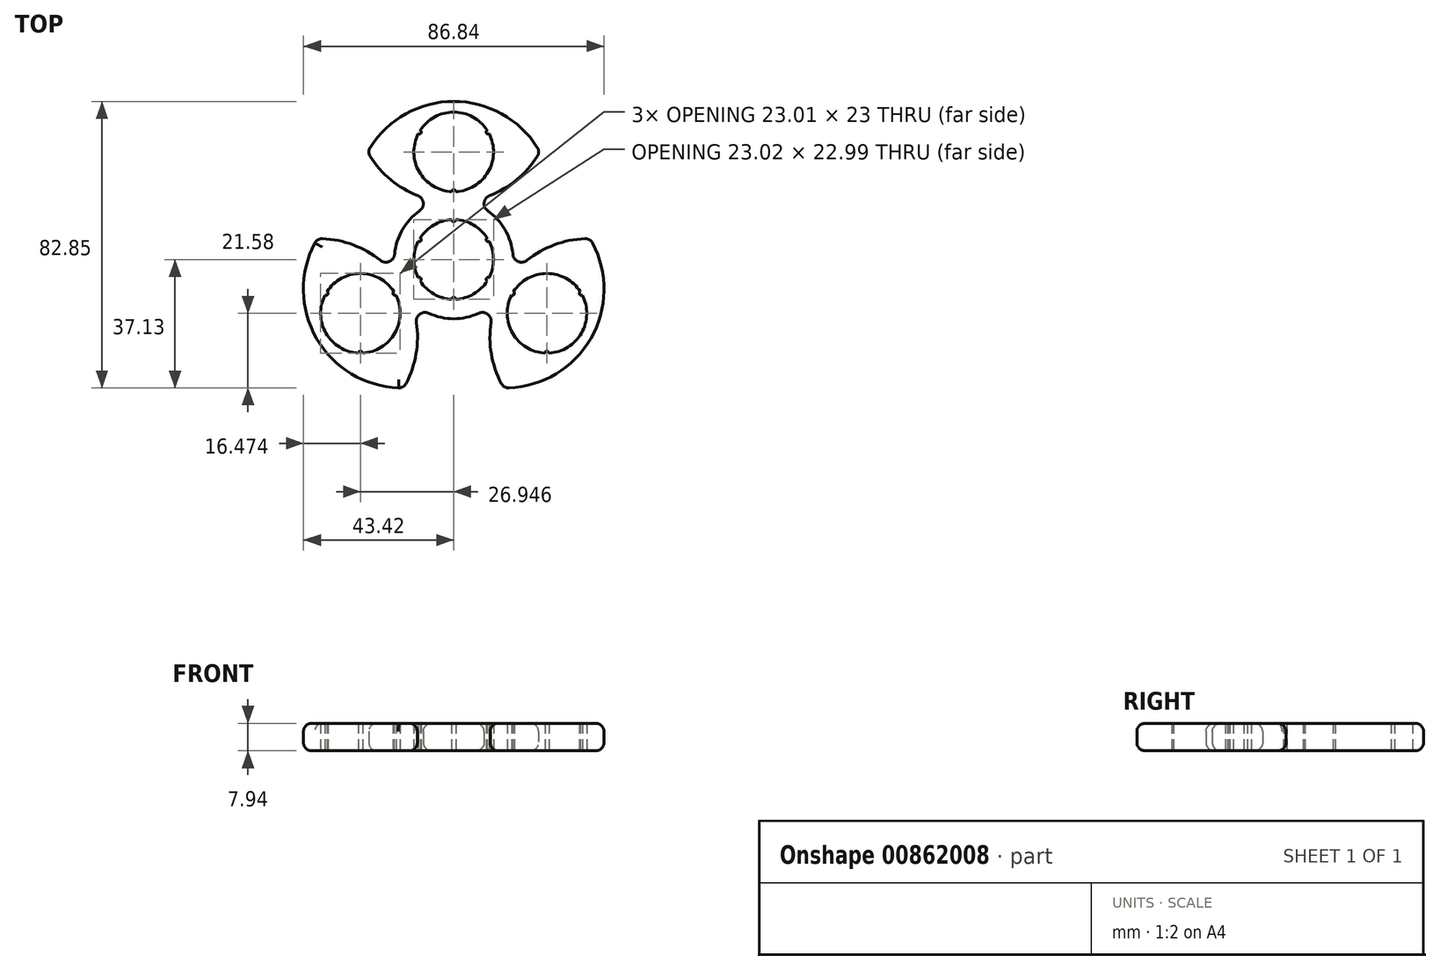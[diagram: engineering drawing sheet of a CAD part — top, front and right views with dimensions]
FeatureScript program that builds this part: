
annotation { "Feature Type Name" : "Feature", "Feature Type Description" : "" }
export const myFeature = defineFeature(function(context is Context, id is Id, definition is map)
    precondition{}
    {
        {
            var Q0;
            Q0=qCreatedBy(makeId("Top.planeOp"),FACE);
            var sketch = newSketch(context, id + "F0", { "sketchPlane" : qUnion([Q0])});
            skCircle(sketch, "E0", {"center": v(0, 0) * mm, "radius": 45.72 * mm, "construction": true});
            skLineSegment(sketch, "E1", {"start": v(0, 0) * mm, "end": v(0, 90.17) * mm, "construction": true});
            skLineSegment(sketch, "E2", {"start": v(0, 0) * mm, "end": v(-73.93, -42.68) * mm, "construction": true});
            skLineSegment(sketch, "E3", {"start": v(0, 0) * mm, "end": v(66.36, -38.31) * mm, "construction": true});
            skArc(sketch, "E4", {"start": v(9.66, 37.37) * mm, "mid": v(0, 42.62) * mm, "end": v(-9.66, 37.37) * mm});
            skArc(sketch, "E5", {"start": v(-0.59, 11.5) * mm, "mid": v(-5.75, 9.97) * mm, "end": v(-9.66, 6.26) * mm});
            skPoint(sketch, "E6", {"position": v(0, 17.14) * mm});
            skArc(sketch, "E7", {"start": v(24.93, 31.12) * mm, "mid": v(0, 45.72) * mm, "end": v(-24.93, 31.12) * mm});
            skPoint(sketch, "E8", {"position": v(0, 45.09) * mm});
            skArc(sketch, "E9", {"start": v(-24.93, 31.12) * mm, "mid": v(-18.76, 23.53) * mm, "end": v(-10.4, 18.47) * mm});
            skLineSegment(sketch, "E10", {"start": v(-41.52, 31.12) * mm, "end": v(42.77, 31.12) * mm, "construction": true});
            skArc(sketch, "E11", {"start": v(-9.86, 14.03) * mm, "mid": v(-14.85, 8.57) * mm, "end": v(-17.08, 1.53) * mm});
            skArc(sketch, "E12.1.0", {"start": v(-39.41, 6.03) * mm, "mid": v(-39.6, -22.86) * mm, "end": v(-14.48, -37.15) * mm});
            skArc(sketch, "E12.1.1", {"start": v(-17.29, -9.3) * mm, "mid": v(-26.95, -4.05) * mm, "end": v(-36.6, -9.3) * mm});
            skArc(sketch, "E12.1.2", {"start": v(-14.48, -37.15) * mm, "mid": v(-11, -28.01) * mm, "end": v(-10.8, -18.24) * mm});
            skArc(sketch, "E12.2.0", {"start": v(14.48, -37.15) * mm, "mid": v(39.6, -22.86) * mm, "end": v(39.41, 6.03) * mm});
            skArc(sketch, "E12.2.1", {"start": v(16.7, -10.32) * mm, "mid": v(16.98, -21.31) * mm, "end": v(26.36, -27.05) * mm});
            skArc(sketch, "E12.2.2", {"start": v(39.41, 6.03) * mm, "mid": v(29.76, 4.48) * mm, "end": v(21.2, -0.23) * mm});
            skArc(sketch, "E13.trimOffspring", {"start": v(10.4, 18.47) * mm, "mid": v(18.76, 23.53) * mm, "end": v(24.93, 31.12) * mm});
            skArc(sketch, "E14.trimOffspring", {"start": v(17.08, 1.53) * mm, "mid": v(14.85, 8.57) * mm, "end": v(9.86, 14.03) * mm});
            skArc(sketch, "E15.trimOffspring", {"start": v(10.8, -18.24) * mm, "mid": v(11, -28.01) * mm, "end": v(14.48, -37.15) * mm});
            skArc(sketch, "E16.trimOffspring", {"start": v(-21.2, -0.23) * mm, "mid": v(-29.76, 4.48) * mm, "end": v(-39.41, 6.03) * mm});
            skArc(sketch, "E17.trimOffspring", {"start": v(-7.22, -15.55) * mm, "mid": v(0, -17.15) * mm, "end": v(7.22, -15.55) * mm});
            skPoint(sketch, "E18.visualSharp", {"position": v(-3.67, 16.75) * mm});
            skArc(sketch, "E18.filletArc", {"start": v(-9.86, 14.03) * mm, "mid": v(-8.8, 16.4) * mm, "end": v(-10.4, 18.47) * mm});
            skPoint(sketch, "E19.visualSharp", {"position": v(3.67, 16.75) * mm});
            skArc(sketch, "E19.filletArc", {"start": v(10.4, 18.47) * mm, "mid": v(8.8, 16.4) * mm, "end": v(9.86, 14.03) * mm});
            skPoint(sketch, "E20.visualSharp", {"position": v(16.34, -5.2) * mm});
            skArc(sketch, "E20.filletArc", {"start": v(17.08, 1.53) * mm, "mid": v(18.6, -0.58) * mm, "end": v(21.2, -0.23) * mm});
            skPoint(sketch, "E21.visualSharp", {"position": v(12.67, -11.55) * mm});
            skArc(sketch, "E21.filletArc", {"start": v(10.8, -18.24) * mm, "mid": v(9.8, -15.83) * mm, "end": v(7.22, -15.55) * mm});
            skPoint(sketch, "E22.visualSharp", {"position": v(-12.67, -11.55) * mm});
            skArc(sketch, "E22.filletArc", {"start": v(-7.22, -15.55) * mm, "mid": v(-9.8, -15.83) * mm, "end": v(-10.8, -18.24) * mm});
            skPoint(sketch, "E23.visualSharp", {"position": v(-16.34, -5.2) * mm});
            skArc(sketch, "E23.filletArc", {"start": v(-21.2, -0.23) * mm, "mid": v(-18.6, -0.58) * mm, "end": v(-17.08, 1.53) * mm});
            skLineSegment(sketch, "E24", {"start": v(0, 31.12) * mm, "end": v(-25.28, 45.7) * mm, "construction": true});
            skLineSegment(sketch, "E25", {"start": v(0, 31.11) * mm, "end": v(24.72, 45.39) * mm, "construction": true});
            skCircle(sketch, "E26", {"center": v(0, 31.12) * mm, "radius": 10.92 * mm, "construction": true});
            skArc(sketch, "E27", {"start": v(0.59, 19.62) * mm, "mid": v(0, 20.2) * mm, "end": v(-0.59, 19.62) * mm});
            skArc(sketch, "E28", {"start": v(-10.25, 36.35) * mm, "mid": v(-9.46, 36.58) * mm, "end": v(-9.66, 37.37) * mm});
            skArc(sketch, "E29", {"start": v(9.66, 37.37) * mm, "mid": v(9.46, 36.58) * mm, "end": v(10.25, 36.35) * mm});
            skArc(sketch, "E30.1.0", {"start": v(-26.36, -27.05) * mm, "mid": v(-26.95, -26.48) * mm, "end": v(-27.53, -27.05) * mm});
            skArc(sketch, "E30.1.1", {"start": v(-37.2, -10.32) * mm, "mid": v(-36.4, -10.1) * mm, "end": v(-36.6, -9.3) * mm});
            skArc(sketch, "E30.1.2", {"start": v(-17.29, -9.3) * mm, "mid": v(-17.49, -10.1) * mm, "end": v(-16.7, -10.32) * mm});
            skArc(sketch, "E30.2.0", {"start": v(36.6, -9.3) * mm, "mid": v(36.4, -10.1) * mm, "end": v(37.2, -10.32) * mm});
            skArc(sketch, "E30.2.1", {"start": v(27.53, -27.05) * mm, "mid": v(26.95, -26.48) * mm, "end": v(26.36, -27.05) * mm});
            skArc(sketch, "E30.2.2", {"start": v(16.7, -10.32) * mm, "mid": v(17.49, -10.1) * mm, "end": v(17.29, -9.3) * mm});
            skArc(sketch, "E31.trimOffspring", {"start": v(-10.25, 36.35) * mm, "mid": v(-9.97, 25.36) * mm, "end": v(-0.59, 19.62) * mm});
            skArc(sketch, "E32.trimOffspring", {"start": v(0.59, 19.62) * mm, "mid": v(9.97, 25.36) * mm, "end": v(10.25, 36.35) * mm});
            skArc(sketch, "E33.trimOffspring", {"start": v(-37.2, -10.32) * mm, "mid": v(-36.91, -21.31) * mm, "end": v(-27.53, -27.05) * mm});
            skArc(sketch, "E34.trimOffspring", {"start": v(-26.36, -27.05) * mm, "mid": v(-16.98, -21.31) * mm, "end": v(-16.7, -10.32) * mm});
            skArc(sketch, "E35.trimOffspring", {"start": v(36.6, -9.3) * mm, "mid": v(26.95, -4.05) * mm, "end": v(17.29, -9.3) * mm});
            skArc(sketch, "E36.trimOffspring", {"start": v(27.53, -27.05) * mm, "mid": v(36.91, -21.31) * mm, "end": v(37.2, -10.32) * mm});
            skCircle(sketch, "E37", {"center": v(0, 0) * mm, "radius": 10.92 * mm, "construction": true});
            skArc(sketch, "E38", {"start": v(-0.59, 11.5) * mm, "mid": v(0, 10.92) * mm, "end": v(0.59, 11.5) * mm});
            skArc(sketch, "E39.1.0", {"start": v(-10.25, 5.24) * mm, "mid": v(-9.46, 5.46) * mm, "end": v(-9.66, 6.26) * mm});
            skArc(sketch, "E39.2.0", {"start": v(-9.66, -6.26) * mm, "mid": v(-9.46, -5.46) * mm, "end": v(-10.25, -5.24) * mm});
            skArc(sketch, "E39.3.0", {"start": v(0.59, -11.5) * mm, "mid": v(0, -10.92) * mm, "end": v(-0.59, -11.5) * mm});
            skArc(sketch, "E39.4.0", {"start": v(10.25, -5.24) * mm, "mid": v(9.46, -5.46) * mm, "end": v(9.66, -6.26) * mm});
            skArc(sketch, "E39.5.0", {"start": v(9.66, 6.26) * mm, "mid": v(9.46, 5.46) * mm, "end": v(10.25, 5.24) * mm});
            skArc(sketch, "E40.trimOffspring", {"start": v(9.66, 6.26) * mm, "mid": v(5.75, 9.97) * mm, "end": v(0.59, 11.5) * mm});
            skArc(sketch, "E41.trimOffspring", {"start": v(10.25, -5.24) * mm, "mid": v(11.5, 0) * mm, "end": v(10.25, 5.24) * mm});
            skArc(sketch, "E42.trimOffspring", {"start": v(0.59, -11.5) * mm, "mid": v(5.75, -9.97) * mm, "end": v(9.66, -6.26) * mm});
            skArc(sketch, "E43.trimOffspring", {"start": v(-9.66, -6.26) * mm, "mid": v(-5.75, -9.97) * mm, "end": v(-0.59, -11.5) * mm});
            skArc(sketch, "E44.trimOffspring", {"start": v(-10.25, 5.24) * mm, "mid": v(-11.5, 0) * mm, "end": v(-10.25, -5.24) * mm});
            skSolve(sketch);
        }
        {
            var Q0;
            Q0 = qSketchRegion(id + "F0", true);
            extrude(context, id + "F1", {"entities" : qUnion([Q0]), "depth" : 7.94 * mm, "offsetDistance" : 25.4 * mm});
        }
        {
            var Q0;
            Q0=makeQuery(id+"F1.opExtrude","CAP_EDGE",EDGE,{"disambiguationData":[OSD([sQuery(id+"F0.wireOp",EDGE,"E12.1.0")])],"isStart":false});
            fillet(context, id + "F2", {"entities" : qUnion([Q0]), "radius" : 2.38 * mm, "tangentPropagation" : true, "allowEdgeOverflow" : false});
        }
        {
            var Q0;
            Q0=makeQuery(id+"F1.opExtrude","CAP_EDGE",EDGE,{"disambiguationData":[OSD([sQuery(id+"F0.wireOp",EDGE,"E12.1.2")])],"isStart":false});
            var Q1;
            Q1=makeQuery(id+"F1.opExtrude","CAP_EDGE",EDGE,{"disambiguationData":[OSD([sQuery(id+"F0.wireOp",EDGE,"E22.filletArc")])],"isStart":false});
            var Q2;
            Q2=makeQuery(id+"F1.opExtrude","CAP_EDGE",EDGE,{"disambiguationData":[OSD([sQuery(id+"F0.wireOp",EDGE,"E17.trimOffspring")])],"isStart":false});
            var Q3;
            Q3=makeQuery(id+"F1.opExtrude","CAP_EDGE",EDGE,{"disambiguationData":[OSD([sQuery(id+"F0.wireOp",EDGE,"E21.filletArc")])],"isStart":false});
            var Q4;
            Q4=makeQuery(id+"F1.opExtrude","CAP_EDGE",EDGE,{"disambiguationData":[OSD([sQuery(id+"F0.wireOp",EDGE,"E15.trimOffspring")])],"isStart":false});
            var Q5;
            Q5=makeQuery(id+"F1.opExtrude","CAP_EDGE",EDGE,{"disambiguationData":[OSD([sQuery(id+"F0.wireOp",EDGE,"E12.2.0")])],"isStart":false});
            var Q6;
            Q6=makeQuery(id+"F1.opExtrude","CAP_EDGE",EDGE,{"disambiguationData":[OSD([sQuery(id+"F0.wireOp",EDGE,"E12.2.2")])],"isStart":false});
            var Q7;
            Q7=makeQuery(id+"F1.opExtrude","CAP_EDGE",EDGE,{"disambiguationData":[OSD([sQuery(id+"F0.wireOp",EDGE,"E20.filletArc")])],"isStart":false});
            var Q8;
            Q8=makeQuery(id+"F1.opExtrude","CAP_EDGE",EDGE,{"disambiguationData":[OSD([sQuery(id+"F0.wireOp",EDGE,"E14.trimOffspring")])],"isStart":false});
            var Q9;
            Q9=makeQuery(id+"F1.opExtrude","CAP_EDGE",EDGE,{"disambiguationData":[OSD([sQuery(id+"F0.wireOp",EDGE,"E19.filletArc")])],"isStart":false});
            var Q10;
            Q10=makeQuery(id+"F1.opExtrude","CAP_EDGE",EDGE,{"disambiguationData":[OSD([sQuery(id+"F0.wireOp",EDGE,"E13.trimOffspring")])],"isStart":false});
            var Q11;
            Q11=makeQuery(id+"F1.opExtrude","CAP_EDGE",EDGE,{"disambiguationData":[OSD([sQuery(id+"F0.wireOp",EDGE,"E7")])],"isStart":false});
            var Q12;
            Q12=makeQuery(id+"F1.opExtrude","CAP_EDGE",EDGE,{"disambiguationData":[OSD([sQuery(id+"F0.wireOp",EDGE,"E9")])],"isStart":false});
            var Q13;
            Q13=makeQuery(id+"F1.opExtrude","CAP_EDGE",EDGE,{"disambiguationData":[OSD([sQuery(id+"F0.wireOp",EDGE,"E18.filletArc")])],"isStart":false});
            var Q14;
            Q14=makeQuery(id+"F1.opExtrude","CAP_EDGE",EDGE,{"disambiguationData":[OSD([sQuery(id+"F0.wireOp",EDGE,"E11")])],"isStart":false});
            var Q15;
            Q15=makeQuery(id+"F1.opExtrude","CAP_EDGE",EDGE,{"disambiguationData":[OSD([sQuery(id+"F0.wireOp",EDGE,"E23.filletArc")])],"isStart":false});
            var Q16;
            Q16=makeQuery(id+"F1.opExtrude","CAP_EDGE",EDGE,{"disambiguationData":[OSD([sQuery(id+"F0.wireOp",EDGE,"E16.trimOffspring")])],"isStart":false});
            fillet(context, id + "F3", {"entities" : qUnion([Q0, Q1, Q2, Q3, Q4, Q5, Q6, Q7, Q8, Q9, Q10, Q11, Q12, Q13, Q14, Q15, Q16]), "radius" : 2.38 * mm, "tangentPropagation" : true, "allowEdgeOverflow" : false});
        }
        {
            var Q0;
            Q0=makeQuery(id+"F1.opExtrude","CAP_EDGE",EDGE,{"disambiguationData":[OSD([sQuery(id+"F0.wireOp",EDGE,"E12.1.0")])],"isStart":true});
            var Q1;
            {var subQ0=sQuery(id+"F0.wireOp",EDGE,"E16.trimOffspring");var subQ1=sQuery(id+"F0.wireOp",EDGE,"E12.1.0");Q1=makeQuery(id+"F3.opFillet","BLEND_EDGE",EDGE,{"blendedFrom":[makeQuery(id+"F1.opExtrude","SWEPT_EDGE",EDGE,{"disambiguationData":[OSD([subQ1,subQ0])]}),makeQuery(id+"F1.opExtrude","CAP_FACE",FACE,{"disambiguationData":[OSD([sQuery(id+"F0.wireOp",EDGE,"E4"),sQuery(id+"F0.wireOp",EDGE,"E5"),sQuery(id+"F0.wireOp",EDGE,"E7"),sQuery(id+"F0.wireOp",EDGE,"E9"),sQuery(id+"F0.wireOp",EDGE,"E11"),subQ1,sQuery(id+"F0.wireOp",EDGE,"E12.1.1"),sQuery(id+"F0.wireOp",EDGE,"E12.1.2"),sQuery(id+"F0.wireOp",EDGE,"E12.2.0"),sQuery(id+"F0.wireOp",EDGE,"E12.2.1"),sQuery(id+"F0.wireOp",EDGE,"E12.2.2"),sQuery(id+"F0.wireOp",EDGE,"E13.trimOffspring"),sQuery(id+"F0.wireOp",EDGE,"E14.trimOffspring"),sQuery(id+"F0.wireOp",EDGE,"E15.trimOffspring"),subQ0,sQuery(id+"F0.wireOp",EDGE,"E17.trimOffspring"),sQuery(id+"F0.wireOp",EDGE,"E18.filletArc"),sQuery(id+"F0.wireOp",EDGE,"E19.filletArc"),sQuery(id+"F0.wireOp",EDGE,"E20.filletArc"),sQuery(id+"F0.wireOp",EDGE,"E21.filletArc"),sQuery(id+"F0.wireOp",EDGE,"E22.filletArc"),sQuery(id+"F0.wireOp",EDGE,"E23.filletArc")])],"isStart":true})],"blendedInto":[makeQuery(id+"F1.opExtrude","CAP_FACE",FACE,{"disambiguationData":[OSD([sQuery(id+"F0.wireOp",EDGE,"E4"),sQuery(id+"F0.wireOp",EDGE,"E5"),sQuery(id+"F0.wireOp",EDGE,"E7"),sQuery(id+"F0.wireOp",EDGE,"E9"),sQuery(id+"F0.wireOp",EDGE,"E11"),subQ1,sQuery(id+"F0.wireOp",EDGE,"E12.1.1"),sQuery(id+"F0.wireOp",EDGE,"E12.1.2"),sQuery(id+"F0.wireOp",EDGE,"E12.2.0"),sQuery(id+"F0.wireOp",EDGE,"E12.2.1"),sQuery(id+"F0.wireOp",EDGE,"E12.2.2"),sQuery(id+"F0.wireOp",EDGE,"E13.trimOffspring"),sQuery(id+"F0.wireOp",EDGE,"E14.trimOffspring"),sQuery(id+"F0.wireOp",EDGE,"E15.trimOffspring"),subQ0,sQuery(id+"F0.wireOp",EDGE,"E17.trimOffspring"),sQuery(id+"F0.wireOp",EDGE,"E18.filletArc"),sQuery(id+"F0.wireOp",EDGE,"E19.filletArc"),sQuery(id+"F0.wireOp",EDGE,"E20.filletArc"),sQuery(id+"F0.wireOp",EDGE,"E21.filletArc"),sQuery(id+"F0.wireOp",EDGE,"E22.filletArc"),sQuery(id+"F0.wireOp",EDGE,"E23.filletArc")])],"isStart":true})]});}
            var Q2;
            Q2=makeQuery(id+"F1.opExtrude","CAP_EDGE",EDGE,{"disambiguationData":[OSD([sQuery(id+"F0.wireOp",EDGE,"E16.trimOffspring")])],"isStart":true});
            var Q3;
            Q3=makeQuery(id+"F1.opExtrude","CAP_EDGE",EDGE,{"disambiguationData":[OSD([sQuery(id+"F0.wireOp",EDGE,"E23.filletArc")])],"isStart":true});
            var Q4;
            Q4=makeQuery(id+"F1.opExtrude","CAP_EDGE",EDGE,{"disambiguationData":[OSD([sQuery(id+"F0.wireOp",EDGE,"E11")])],"isStart":true});
            var Q5;
            Q5=makeQuery(id+"F1.opExtrude","CAP_EDGE",EDGE,{"disambiguationData":[OSD([sQuery(id+"F0.wireOp",EDGE,"E18.filletArc")])],"isStart":true});
            var Q6;
            Q6=makeQuery(id+"F1.opExtrude","CAP_EDGE",EDGE,{"disambiguationData":[OSD([sQuery(id+"F0.wireOp",EDGE,"E9")])],"isStart":true});
            var Q7;
            Q7=makeQuery(id+"F1.opExtrude","CAP_EDGE",EDGE,{"disambiguationData":[OSD([sQuery(id+"F0.wireOp",EDGE,"E7")])],"isStart":true});
            var Q8;
            Q8=makeQuery(id+"F1.opExtrude","CAP_EDGE",EDGE,{"disambiguationData":[OSD([sQuery(id+"F0.wireOp",EDGE,"E13.trimOffspring")])],"isStart":true});
            var Q9;
            Q9=makeQuery(id+"F1.opExtrude","CAP_EDGE",EDGE,{"disambiguationData":[OSD([sQuery(id+"F0.wireOp",EDGE,"E19.filletArc")])],"isStart":true});
            var Q10;
            Q10=makeQuery(id+"F1.opExtrude","CAP_EDGE",EDGE,{"disambiguationData":[OSD([sQuery(id+"F0.wireOp",EDGE,"E14.trimOffspring")])],"isStart":true});
            var Q11;
            Q11=makeQuery(id+"F1.opExtrude","CAP_EDGE",EDGE,{"disambiguationData":[OSD([sQuery(id+"F0.wireOp",EDGE,"E20.filletArc")])],"isStart":true});
            var Q12;
            Q12=makeQuery(id+"F1.opExtrude","CAP_EDGE",EDGE,{"disambiguationData":[OSD([sQuery(id+"F0.wireOp",EDGE,"E12.2.2")])],"isStart":true});
            var Q13;
            Q13=makeQuery(id+"F1.opExtrude","CAP_EDGE",EDGE,{"disambiguationData":[OSD([sQuery(id+"F0.wireOp",EDGE,"E12.2.0")])],"isStart":true});
            var Q14;
            Q14=makeQuery(id+"F1.opExtrude","CAP_EDGE",EDGE,{"disambiguationData":[OSD([sQuery(id+"F0.wireOp",EDGE,"E15.trimOffspring")])],"isStart":true});
            var Q15;
            Q15=makeQuery(id+"F1.opExtrude","CAP_EDGE",EDGE,{"disambiguationData":[OSD([sQuery(id+"F0.wireOp",EDGE,"E21.filletArc")])],"isStart":true});
            var Q16;
            Q16=makeQuery(id+"F1.opExtrude","CAP_EDGE",EDGE,{"disambiguationData":[OSD([sQuery(id+"F0.wireOp",EDGE,"E17.trimOffspring")])],"isStart":true});
            var Q17;
            Q17=makeQuery(id+"F1.opExtrude","CAP_EDGE",EDGE,{"disambiguationData":[OSD([sQuery(id+"F0.wireOp",EDGE,"E22.filletArc")])],"isStart":true});
            var Q18;
            Q18=makeQuery(id+"F1.opExtrude","CAP_EDGE",EDGE,{"disambiguationData":[OSD([sQuery(id+"F0.wireOp",EDGE,"E12.1.2")])],"isStart":true});
            var Q19;
            {var subQ0=sQuery(id+"F0.wireOp",EDGE,"E12.1.2");var subQ1=sQuery(id+"F0.wireOp",EDGE,"E12.1.0");Q19=makeQuery(id+"F3.opFillet","BLEND_EDGE",EDGE,{"blendedFrom":[makeQuery(id+"F1.opExtrude","SWEPT_EDGE",EDGE,{"disambiguationData":[OSD([subQ1,subQ0])]}),makeQuery(id+"F1.opExtrude","CAP_FACE",FACE,{"disambiguationData":[OSD([sQuery(id+"F0.wireOp",EDGE,"E4"),sQuery(id+"F0.wireOp",EDGE,"E5"),sQuery(id+"F0.wireOp",EDGE,"E7"),sQuery(id+"F0.wireOp",EDGE,"E9"),sQuery(id+"F0.wireOp",EDGE,"E11"),subQ1,sQuery(id+"F0.wireOp",EDGE,"E12.1.1"),subQ0,sQuery(id+"F0.wireOp",EDGE,"E12.2.0"),sQuery(id+"F0.wireOp",EDGE,"E12.2.1"),sQuery(id+"F0.wireOp",EDGE,"E12.2.2"),sQuery(id+"F0.wireOp",EDGE,"E13.trimOffspring"),sQuery(id+"F0.wireOp",EDGE,"E14.trimOffspring"),sQuery(id+"F0.wireOp",EDGE,"E15.trimOffspring"),sQuery(id+"F0.wireOp",EDGE,"E16.trimOffspring"),sQuery(id+"F0.wireOp",EDGE,"E17.trimOffspring"),sQuery(id+"F0.wireOp",EDGE,"E18.filletArc"),sQuery(id+"F0.wireOp",EDGE,"E19.filletArc"),sQuery(id+"F0.wireOp",EDGE,"E20.filletArc"),sQuery(id+"F0.wireOp",EDGE,"E21.filletArc"),sQuery(id+"F0.wireOp",EDGE,"E22.filletArc"),sQuery(id+"F0.wireOp",EDGE,"E23.filletArc")])],"isStart":true})],"blendedInto":[makeQuery(id+"F1.opExtrude","CAP_FACE",FACE,{"disambiguationData":[OSD([sQuery(id+"F0.wireOp",EDGE,"E4"),sQuery(id+"F0.wireOp",EDGE,"E5"),sQuery(id+"F0.wireOp",EDGE,"E7"),sQuery(id+"F0.wireOp",EDGE,"E9"),sQuery(id+"F0.wireOp",EDGE,"E11"),subQ1,sQuery(id+"F0.wireOp",EDGE,"E12.1.1"),subQ0,sQuery(id+"F0.wireOp",EDGE,"E12.2.0"),sQuery(id+"F0.wireOp",EDGE,"E12.2.1"),sQuery(id+"F0.wireOp",EDGE,"E12.2.2"),sQuery(id+"F0.wireOp",EDGE,"E13.trimOffspring"),sQuery(id+"F0.wireOp",EDGE,"E14.trimOffspring"),sQuery(id+"F0.wireOp",EDGE,"E15.trimOffspring"),sQuery(id+"F0.wireOp",EDGE,"E16.trimOffspring"),sQuery(id+"F0.wireOp",EDGE,"E17.trimOffspring"),sQuery(id+"F0.wireOp",EDGE,"E18.filletArc"),sQuery(id+"F0.wireOp",EDGE,"E19.filletArc"),sQuery(id+"F0.wireOp",EDGE,"E20.filletArc"),sQuery(id+"F0.wireOp",EDGE,"E21.filletArc"),sQuery(id+"F0.wireOp",EDGE,"E22.filletArc"),sQuery(id+"F0.wireOp",EDGE,"E23.filletArc")])],"isStart":true})]});}
            var Q20;
            Q20=makeQuery(id+"F1.opExtrude","SWEPT_FACE",FACE,{"disambiguationData":[OSD([sQuery(id+"F0.wireOp",EDGE,"E13.trimOffspring")])]});
            fillet(context, id + "F4", {"entities" : qUnion([Q0, Q1, Q2, Q3, Q4, Q5, Q6, Q7, Q8, Q9, Q10, Q11, Q12, Q13, Q14, Q15, Q16, Q17, Q18, Q19, Q20]), "radius" : 2.38 * mm, "tangentPropagation" : true, "allowEdgeOverflow" : false});
        }
        {
            var Q0;
            Q0=makeQuery(id+"F3.opFillet","BLEND_EDGE",EDGE,{"blendedFrom":[makeQuery(id+"F1.opExtrude","CAP_EDGE",EDGE,{"disambiguationData":[OSD([sQuery(id+"F0.wireOp",EDGE,"E7")])],"isStart":false}),makeQuery(id+"F1.opExtrude","CAP_EDGE",EDGE,{"disambiguationData":[OSD([sQuery(id+"F0.wireOp",EDGE,"E13.trimOffspring")])],"isStart":false})],"blendedInto":[]});
            var Q1;
            Q1=makeQuery(id+"F4.opFillet","BLEND_EDGE",EDGE,{"blendedFrom":[makeQuery(id+"F1.opExtrude","CAP_EDGE",EDGE,{"disambiguationData":[OSD([sQuery(id+"F0.wireOp",EDGE,"E7")])],"isStart":true}),makeQuery(id+"F1.opExtrude","CAP_EDGE",EDGE,{"disambiguationData":[OSD([sQuery(id+"F0.wireOp",EDGE,"E9")])],"isStart":true})],"blendedInto":[]});
            var Q2;
            Q2=makeQuery(id+"F1.opExtrude","SWEPT_EDGE",EDGE,{"disambiguationData":[OSD([sQuery(id+"F0.wireOp",EDGE,"E7"),sQuery(id+"F0.wireOp",EDGE,"E9")])]});
            var Q3;
            Q3=makeQuery(id+"F3.opFillet","BLEND_EDGE",EDGE,{"blendedFrom":[makeQuery(id+"F1.opExtrude","CAP_EDGE",EDGE,{"disambiguationData":[OSD([sQuery(id+"F0.wireOp",EDGE,"E7")])],"isStart":false}),makeQuery(id+"F1.opExtrude","CAP_EDGE",EDGE,{"disambiguationData":[OSD([sQuery(id+"F0.wireOp",EDGE,"E9")])],"isStart":false})],"blendedInto":[]});
            var Q4;
            Q4=makeQuery(id+"F4.opFillet","BLEND_EDGE",EDGE,{"blendedFrom":[makeQuery(id+"F1.opExtrude","CAP_EDGE",EDGE,{"disambiguationData":[OSD([sQuery(id+"F0.wireOp",EDGE,"E12.2.0")])],"isStart":true}),makeQuery(id+"F1.opExtrude","CAP_EDGE",EDGE,{"disambiguationData":[OSD([sQuery(id+"F0.wireOp",EDGE,"E15.trimOffspring")])],"isStart":true})],"blendedInto":[]});
            var Q5;
            Q5=makeQuery(id+"F1.opExtrude","SWEPT_EDGE",EDGE,{"disambiguationData":[OSD([sQuery(id+"F0.wireOp",EDGE,"E12.2.0"),sQuery(id+"F0.wireOp",EDGE,"E15.trimOffspring")])]});
            var Q6;
            Q6=makeQuery(id+"F3.opFillet","BLEND_EDGE",EDGE,{"blendedFrom":[makeQuery(id+"F1.opExtrude","CAP_EDGE",EDGE,{"disambiguationData":[OSD([sQuery(id+"F0.wireOp",EDGE,"E12.2.0")])],"isStart":false}),makeQuery(id+"F1.opExtrude","CAP_EDGE",EDGE,{"disambiguationData":[OSD([sQuery(id+"F0.wireOp",EDGE,"E15.trimOffspring")])],"isStart":false})],"blendedInto":[]});
            var Q7;
            Q7=makeQuery(id+"F4.opFillet","BLEND_EDGE",EDGE,{"blendedFrom":[makeQuery(id+"F1.opExtrude","CAP_EDGE",EDGE,{"disambiguationData":[OSD([sQuery(id+"F0.wireOp",EDGE,"E12.2.0")])],"isStart":true}),makeQuery(id+"F1.opExtrude","CAP_EDGE",EDGE,{"disambiguationData":[OSD([sQuery(id+"F0.wireOp",EDGE,"E12.2.2")])],"isStart":true})],"blendedInto":[]});
            var Q8;
            Q8=makeQuery(id+"F1.opExtrude","SWEPT_EDGE",EDGE,{"disambiguationData":[OSD([sQuery(id+"F0.wireOp",EDGE,"E12.2.0"),sQuery(id+"F0.wireOp",EDGE,"E12.2.2")])]});
            var Q9;
            Q9=makeQuery(id+"F3.opFillet","BLEND_EDGE",EDGE,{"blendedFrom":[makeQuery(id+"F1.opExtrude","CAP_EDGE",EDGE,{"disambiguationData":[OSD([sQuery(id+"F0.wireOp",EDGE,"E12.2.0")])],"isStart":false}),makeQuery(id+"F1.opExtrude","CAP_EDGE",EDGE,{"disambiguationData":[OSD([sQuery(id+"F0.wireOp",EDGE,"E12.2.2")])],"isStart":false})],"blendedInto":[]});
            fillet(context, id + "F5", {"entities" : qUnion([Q0, Q1, Q2, Q3, Q4, Q5, Q6, Q7, Q8, Q9]), "radius" : 2.38 * mm, "tangentPropagation" : true, "allowEdgeOverflow" : false});
        }
    });
